# Revit family: QF_ELECTROLUXPROFESSIONAL_602404
name_source: partatom
category: Specialty Equipment
units: mm (PartAtom-declared; Revit-internal decimal feet)

## family parameters
Cut with Voids When Loaded = No
Enable Cutting in Views = No
Host = Face
Maintain Annotation Orientation = No
Part Type = Normal
Room Calculation Point = No
Round Connector Dimension = Use Diameter
Shared = No

## types (1)
- ADV1552-B
    Controller_Height = 98 mm  [stored 0.321522 ft]
    Controller_Width = 228 mm  [stored 0.748031 ft]
    Cycle = 50 Hz
    Default Elevation = 1219.2 mm  [stored 4 ft]
    Depth = 340 mm  [stored 1.11549 ft]
    Depth Actual = 340 mm  [stored 1.11549 ft]
    Height = 172 mm  [stored 0.564304 ft]
    Height Actual = 172 mm  [stored 0.564304 ft]
    Item Number = ADV1552-B
    Length Actual = 340 mm  [stored 1.11549 ft]
    Manufacturer = ADVENTYS
    Model = GL650FLR
    Phase = 1
    URL = https://adventys.com
    Volts = 220 V
    Watts = 650 W
    Weight = 8
    Width = 340 mm  [stored 1.11549 ft]

note: [stored X ft] marks values corroborated as IEEE doubles in the binary element streams (Revit-internal decimal feet)

## geometry (parser evidence)
native form markers: Blend x4
no freeform markers — native parametric forms only
